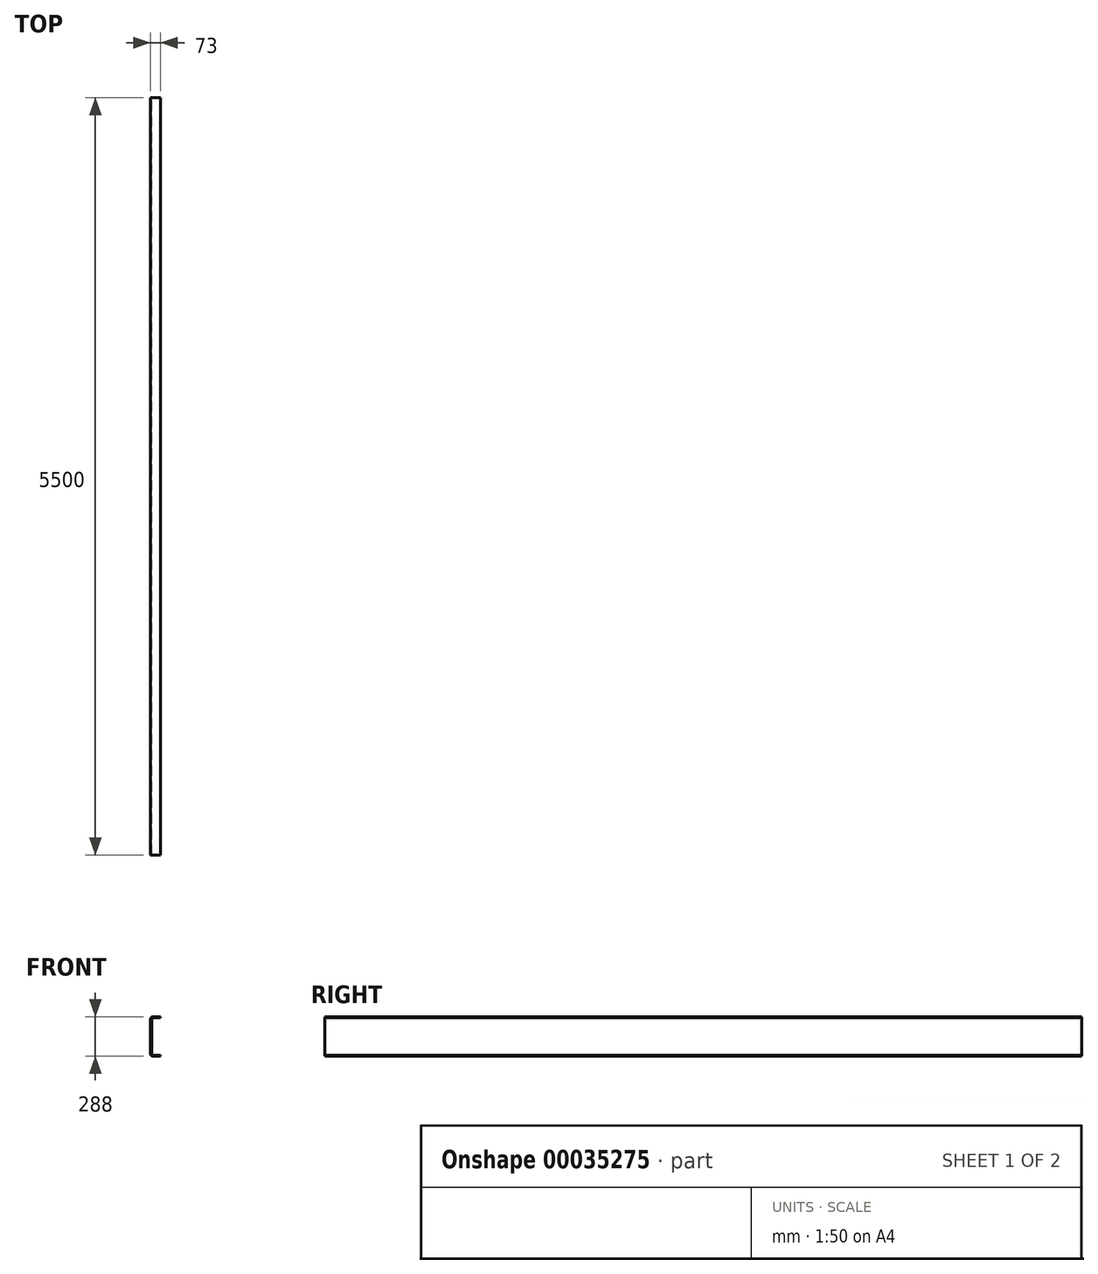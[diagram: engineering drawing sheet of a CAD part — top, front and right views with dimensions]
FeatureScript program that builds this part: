
annotation { "Feature Type Name" : "Feature", "Feature Type Description" : "" }
export const myFeature = defineFeature(function(context is Context, id is Id, definition is map)
    precondition{}
    {
        {
            var Q0;
            Q0=qCreatedBy(makeId("Front.planeOp"),FACE);
            var sketch = newSketch(context, id + "F0", { "sketchPlane" : qUnion([Q0])});
            skLineSegment(sketch, "E0", {"start": v(0, 20) * mm, "end": v(0, 268) * mm});
            skLineSegment(sketch, "E1", {"start": v(20, 288) * mm, "end": v(73, 288) * mm});
            skLineSegment(sketch, "E2", {"start": v(73, 288) * mm, "end": v(73, 280) * mm});
            skLineSegment(sketch, "E3", {"start": v(73, 280) * mm, "end": v(20, 280) * mm});
            skLineSegment(sketch, "E4", {"start": v(8, 268) * mm, "end": v(8, 20) * mm});
            skLineSegment(sketch, "E5", {"start": v(20, 8) * mm, "end": v(73, 8) * mm});
            skLineSegment(sketch, "E6", {"start": v(73, 8) * mm, "end": v(73, 0) * mm});
            skLineSegment(sketch, "E7", {"start": v(73, 0) * mm, "end": v(20, 0) * mm});
            skPoint(sketch, "E8.visualSharp", {"position": v(8, 280) * mm});
            skArc(sketch, "E8.filletArc", {"start": v(20, 280) * mm, "mid": v(11.51, 276.49) * mm, "end": v(8, 268) * mm});
            skPoint(sketch, "E9.visualSharp", {"position": v(8, 8) * mm});
            skArc(sketch, "E9.filletArc", {"start": v(8, 20) * mm, "mid": v(11.51, 11.51) * mm, "end": v(20, 8) * mm});
            skPoint(sketch, "E10.visualSharp", {"position": v(0, 288) * mm});
            skArc(sketch, "E10.filletArc", {"start": v(20, 288) * mm, "mid": v(5.86, 282.14) * mm, "end": v(0, 268) * mm});
            skPoint(sketch, "E11.visualSharp", {"position": v(0, 0) * mm});
            skArc(sketch, "E11.filletArc", {"start": v(0, 20) * mm, "mid": v(5.86, 5.86) * mm, "end": v(20, 0) * mm});
            skSolve(sketch);
        }
        {
            var Q0;
            Q0=makeQuery(id+"F0.imprint","IMPRINT",FACE,{"disambiguationData":[TD([[makeQuery(id+"F0.imprint","IMPRINT",EDGE,{"derivedFrom":sQuery(id+"F0.wireOp",EDGE,"E0")}),-1.0]])]});
            extrude(context, id + "F1", {"entities" : qUnion([Q0]), "depth" : 5500 * mm});
        }
    });
